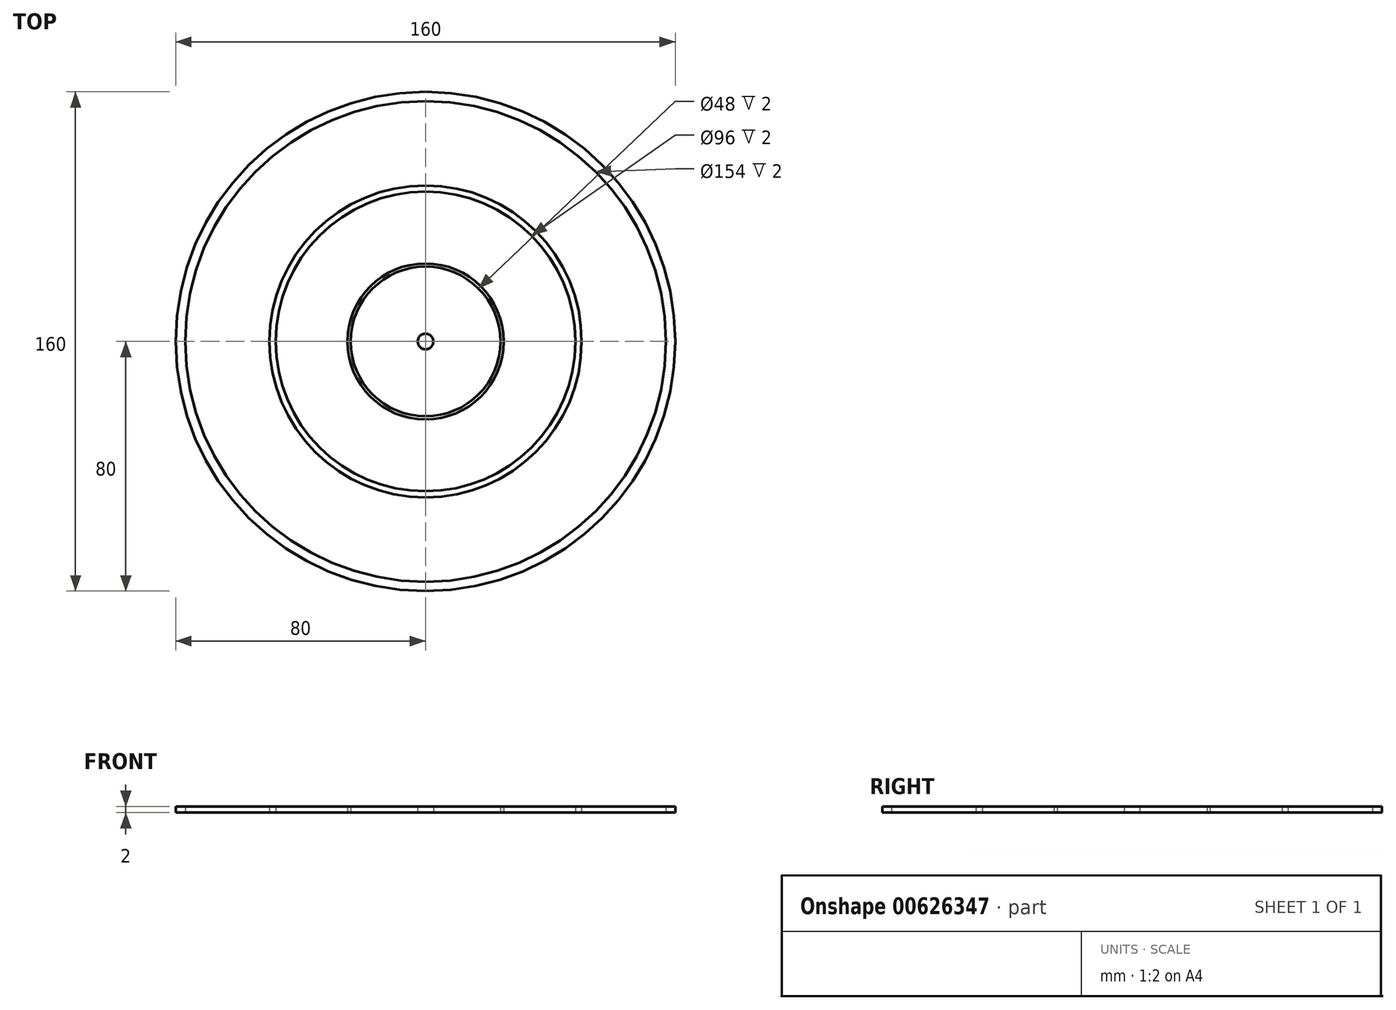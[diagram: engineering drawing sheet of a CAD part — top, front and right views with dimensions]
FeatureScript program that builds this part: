
annotation { "Feature Type Name" : "Feature", "Feature Type Description" : "" }
export const myFeature = defineFeature(function(context is Context, id is Id, definition is map)
    precondition{}
    {
        {
            var Q0;
            Q0=qCreatedBy(makeId("Top.planeOp"),FACE);
            var sketch = newSketch(context, id + "F0", { "sketchPlane" : qUnion([Q0])});
            skCircle(sketch, "E0", {"center": v(0, 0) * mm, "radius": 80 * mm});
            skCircle(sketch, "E1", {"center": v(0, 0) * mm, "radius": 77 * mm});
            skCircle(sketch, "E2", {"center": v(0, 0) * mm, "radius": 50 * mm});
            skCircle(sketch, "E3", {"center": v(0, 0) * mm, "radius": 48 * mm});
            skCircle(sketch, "E4", {"center": v(0, 0) * mm, "radius": 2.5 * mm});
            skCircle(sketch, "E5", {"center": v(0, 0) * mm, "radius": 25 * mm});
            skCircle(sketch, "E6", {"center": v(0, 0) * mm, "radius": 24 * mm});
            skSolve(sketch);
        }
        {
            var Q0;
            Q0=makeQuery(id+"F0.imprint","IMPRINT",FACE,{"disambiguationData":[TD([[makeQuery(id+"F0.imprint","IMPRINT",EDGE,{"derivedFrom":sQuery(id+"F0.wireOp",EDGE,"E2")}),1.0]])]});
            var Q1;
            Q1=makeQuery(id+"F0.imprint","IMPRINT",FACE,{"disambiguationData":[TD([[makeQuery(id+"F0.imprint","IMPRINT",EDGE,{"derivedFrom":sQuery(id+"F0.wireOp",EDGE,"E0")}),1.0]])]});
            var Q2;
            Q2=makeQuery(id+"F0.imprint","IMPRINT",FACE,{"disambiguationData":[TD([[makeQuery(id+"F0.imprint","IMPRINT",EDGE,{"derivedFrom":sQuery(id+"F0.wireOp",EDGE,"E5")}),1.0]])]});
            var Q3;
            Q3=makeQuery(id+"F0.imprint","IMPRINT",FACE,{"disambiguationData":[TD([[makeQuery(id+"F0.imprint","IMPRINT",EDGE,{"derivedFrom":sQuery(id+"F0.wireOp",EDGE,"E4")}),1.0]])]});
            extrude(context, id + "F1", {"entities" : qUnion([Q0, Q1, Q2, Q3]), "depth" : 2 * mm, "offsetDistance" : 25 * mm});
        }
    });
